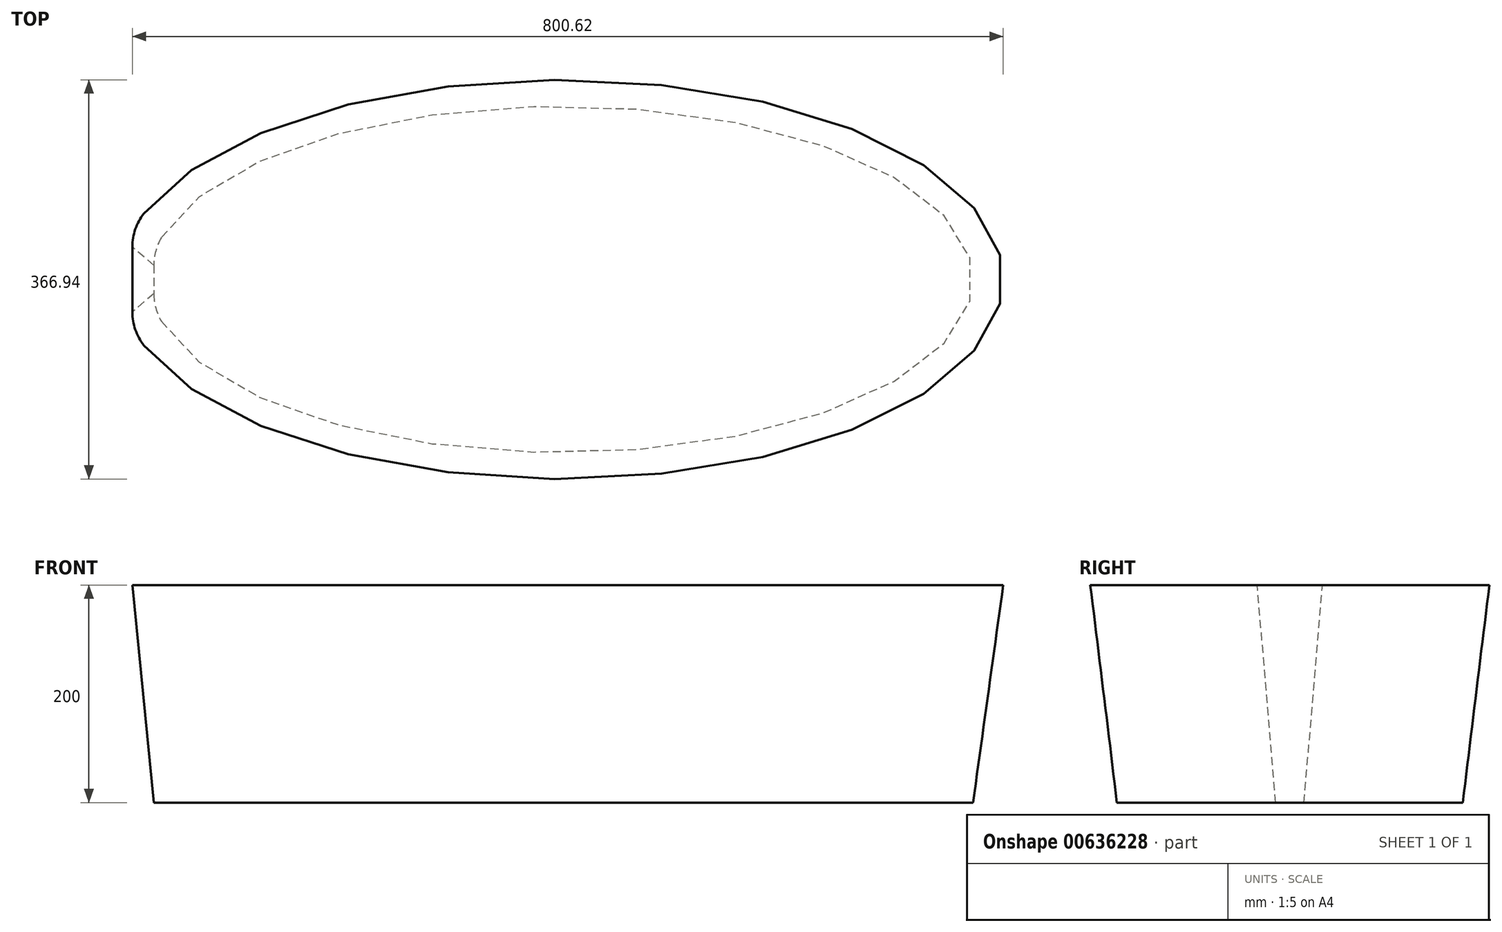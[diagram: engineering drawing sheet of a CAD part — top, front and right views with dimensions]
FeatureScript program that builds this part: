
annotation { "Feature Type Name" : "Feature", "Feature Type Description" : "" }
export const myFeature = defineFeature(function(context is Context, id is Id, definition is map)
    precondition{}
    {
        {
            var Q0;
            Q0=qCreatedBy(makeId("Top.planeOp"),FACE);
            cPlane(context, id + "F0", {"entities" : qUnion([Q0]), "cplaneType" : CPlaneType.OFFSET, "offset" : 200 * mm, "width" : 150 * mm, "height" : 150 * mm});
        }
        {
            var Q0;
            Q0=qCreatedBy(makeId("Top.planeOp"),FACE);
            var sketch = newSketch(context, id + "F1", { "sketchPlane" : qUnion([Q0])});
            skEllipticalArc(sketch, "E0", {});
            skLineSegment(sketch, "E1", {"start": v(-374.43, 13.02) * mm, "end": v(-374.43, -13.02) * mm});
            skPoint(sketch, "E2.visualSharp", {"position": v(-374.43, -23.87) * mm});
            skArc(sketch, "E2.filletArc", {"start": v(-374.43, -13.02) * mm, "mid": v(-372.64, -26.3) * mm, "end": v(-367.38, -38.63) * mm});
            skPoint(sketch, "E3.visualSharp", {"position": v(-374.43, 23.87) * mm});
            skArc(sketch, "E3.filletArc", {"start": v(-367.38, 38.63) * mm, "mid": v(-372.64, 26.3) * mm, "end": v(-374.43, 13.02) * mm});
            const initialGuessF1  = {"E0": [0, 0, 1, 0, 0.3787200450897217, 0.1590357558948842, 3.3869780871706725, 2.896207220008914]};
            skSetInitialGuess(sketch, initialGuessF1);
            skSolve(sketch);
        }
        {
            var Q0;
            Q0=qCreatedBy(id+"F0.planeOp",FACE);
            var sketch = newSketch(context, id + "F2", { "sketchPlane" : qUnion([Q0])});
            skEllipticalArc(sketch, "E4", {});
            skLineSegment(sketch, "E5", {"start": v(-394.15, 29.96) * mm, "end": v(-394.15, -29.96) * mm});
            skPoint(sketch, "E6.visualSharp", {"position": v(-394.15, 44.83) * mm});
            skArc(sketch, "E6.filletArc", {"start": v(-383.66, 60.6) * mm, "mid": v(-391.45, 46.15) * mm, "end": v(-394.15, 29.96) * mm});
            skPoint(sketch, "E7.visualSharp", {"position": v(-394.15, -44.83) * mm});
            skArc(sketch, "E7.filletArc", {"start": v(-394.15, -29.96) * mm, "mid": v(-391.45, -46.15) * mm, "end": v(-383.66, -60.6) * mm});
            const initialGuessF2  = {"E4": [0, 0, 1, 0, 0.4064699113368988, 0.18346900201131028, 3.4781621610362845, 2.8050231461433017]};
            skSetInitialGuess(sketch, initialGuessF2);
            skSolve(sketch);
        }
        {
            var Q0;
            Q0=makeQuery(id+"F1.imprint","IMPRINT",FACE,{"disambiguationData":[TD([[makeQuery(id+"F1.imprint","IMPRINT",EDGE,{"derivedFrom":sQuery(id+"F1.wireOp",EDGE,"E0")}),1.0]])]});
            var Q1;
            Q1=makeQuery(id+"F2.imprint","IMPRINT",FACE,{"disambiguationData":[TD([[makeQuery(id+"F2.imprint","IMPRINT",EDGE,{"derivedFrom":sQuery(id+"F2.wireOp",EDGE,"E4")}),1.0]])]});
            loft(context, id + "F3", {"sheetProfilesArray" : [{ "sheetProfileEntities" : qUnion([Q0]) }, { "sheetProfileEntities" : qUnion([Q1]) }]});
        }
    });
